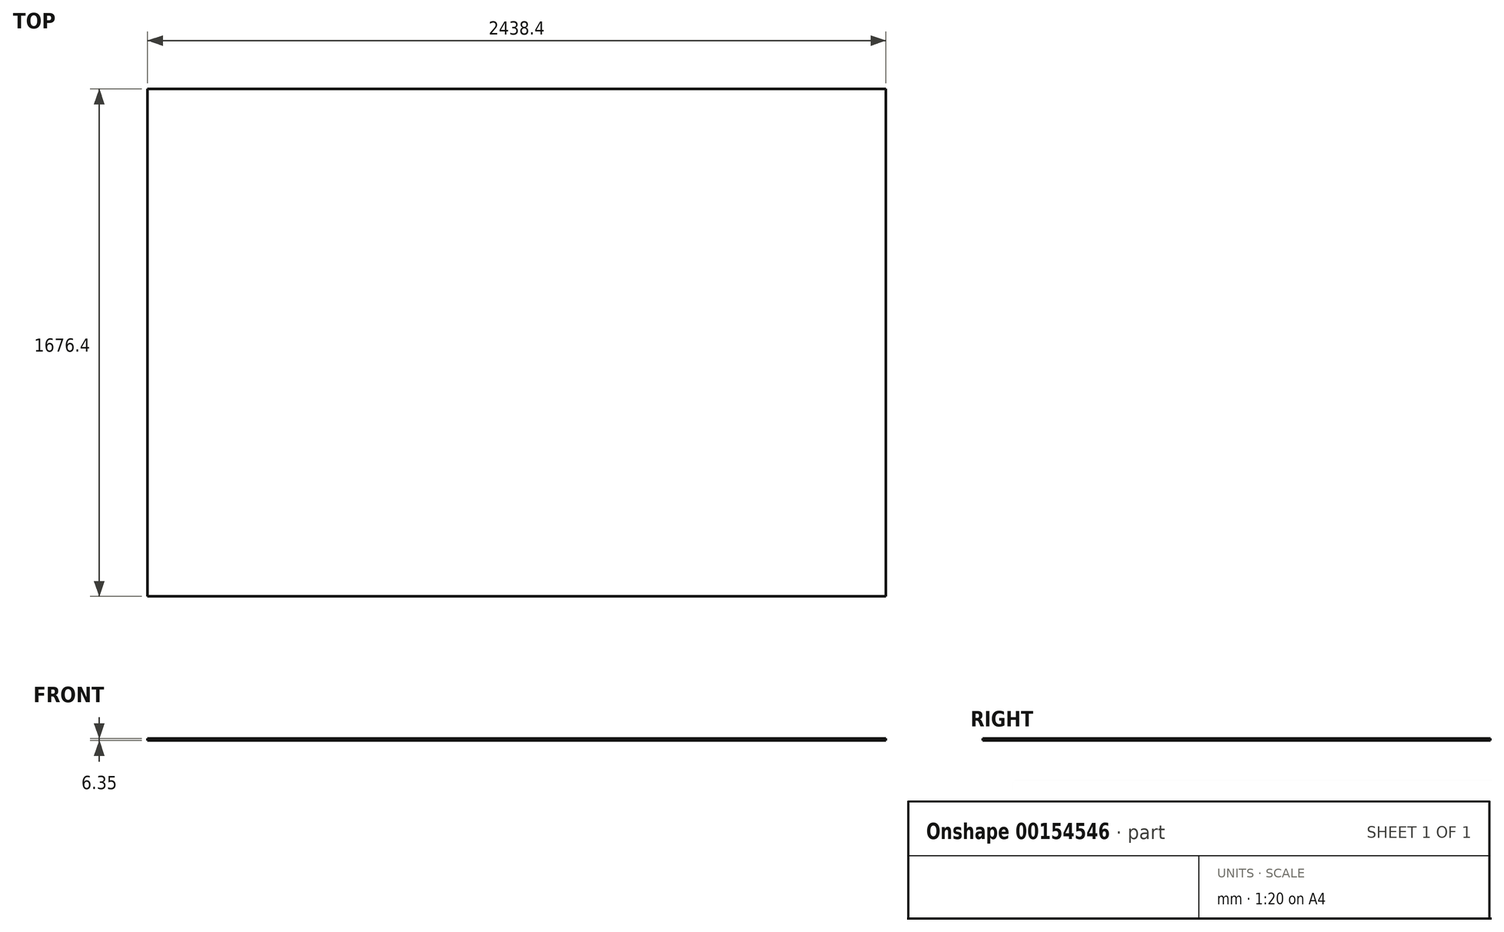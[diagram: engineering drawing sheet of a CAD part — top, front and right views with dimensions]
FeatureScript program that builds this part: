
annotation { "Feature Type Name" : "Feature", "Feature Type Description" : "" }
export const myFeature = defineFeature(function(context is Context, id is Id, definition is map)
    precondition{}
    {
        {
            var Q0;
            Q0=qCreatedBy(makeId("Top.planeOp"),FACE);
            var sketch = newSketch(context, id + "F0", { "sketchPlane" : qUnion([Q0])});
            skLineSegment(sketch, "E0.bottom", {"start": v(1219.2, 838.2) * mm, "end": v(-1219.2, 838.2) * mm});
            skLineSegment(sketch, "E0.top", {"start": v(1219.2, -838.2) * mm, "end": v(-1219.2, -838.2) * mm});
            skLineSegment(sketch, "E0.left", {"start": v(1219.2, 838.2) * mm, "end": v(1219.2, -838.2) * mm});
            skLineSegment(sketch, "E0.right", {"start": v(-1219.2, 838.2) * mm, "end": v(-1219.2, -838.2) * mm});
            skPoint(sketch, "E0.middle", {"position": v(0, 0) * mm});
            skSolve(sketch);
        }
        {
            var Q0;
            Q0=makeQuery(id+"F0.imprint","IMPRINT",FACE,{"disambiguationData":[TD([[makeQuery(id+"F0.imprint","IMPRINT",EDGE,{"derivedFrom":sQuery(id+"F0.wireOp",EDGE,"E0.bottom")}),1.0]])]});
            extrude(context, id + "F1", {"entities" : qUnion([Q0]), "depth" : 6.35 * mm});
        }
    });
